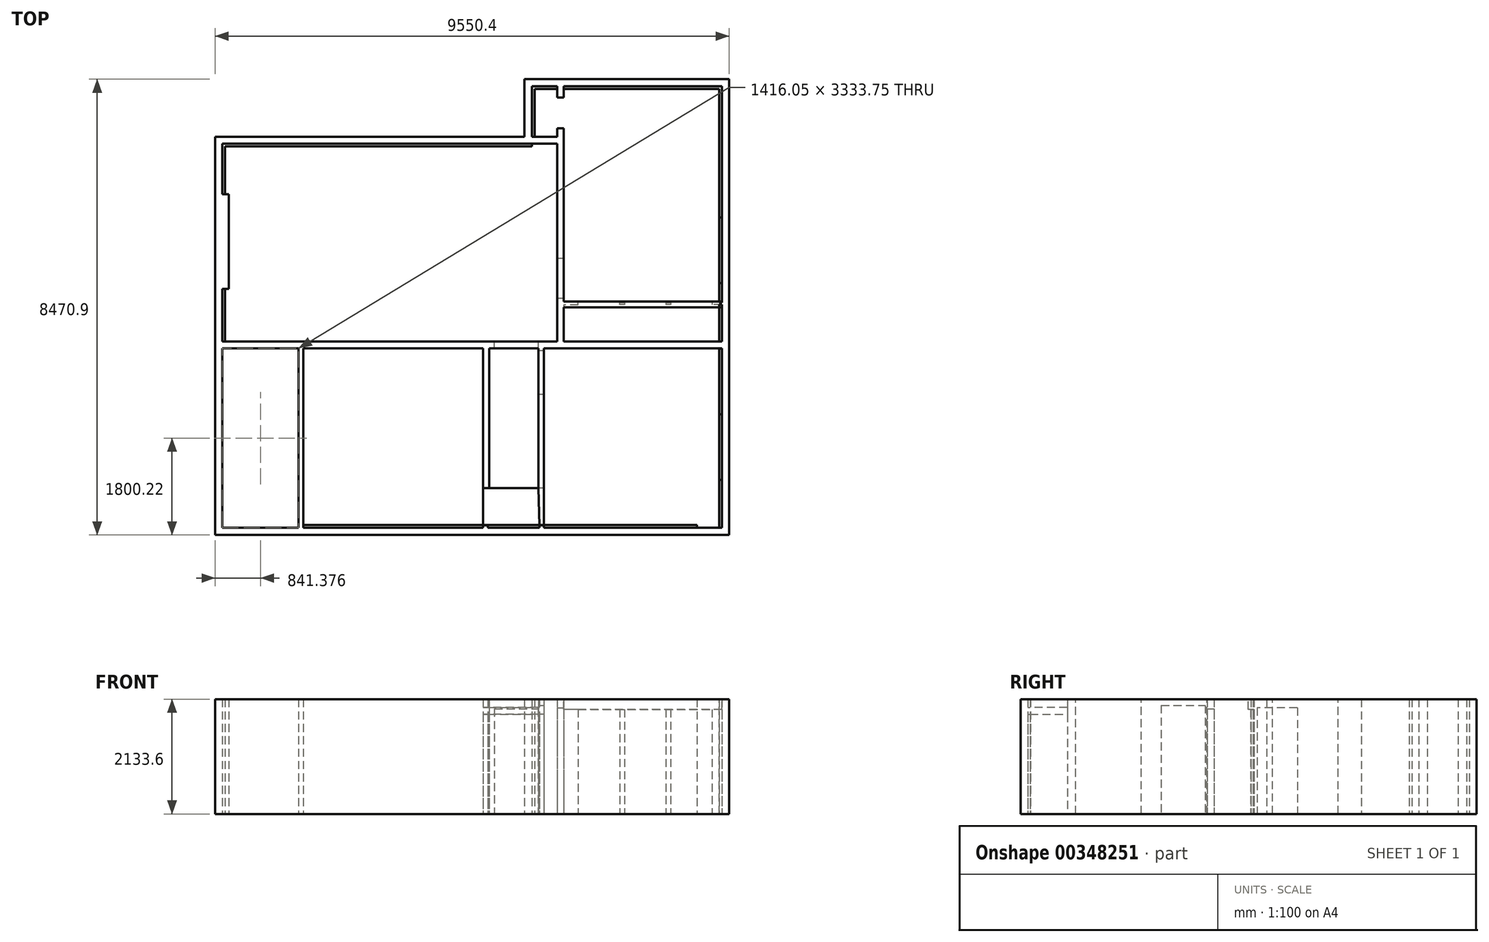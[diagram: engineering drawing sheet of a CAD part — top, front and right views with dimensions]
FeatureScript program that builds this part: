
annotation { "Feature Type Name" : "Feature", "Feature Type Description" : "" }
export const myFeature = defineFeature(function(context is Context, id is Id, definition is map)
    precondition{}
    {
        {
            var Q0;
            Q0=qCreatedBy(makeId("Top.planeOp"),FACE);
            var sketch = newSketch(context, id + "F0", { "sketchPlane" : qUnion([Q0])});
            skLineSegment(sketch, "E0", {"start": v(-2388.66, -7788.34) * mm, "end": v(2665.94, -7788.34) * mm});
            skLineSegment(sketch, "E1", {"start": v(-2388.66, -4111.7) * mm, "end": v(3831.17, -4111.7) * mm});
            skLineSegment(sketch, "E2", {"start": v(-2388.66, -4111.7) * mm, "end": v(-2388.66, -5051.5) * mm});
            skLineSegment(sketch, "E3", {"start": v(-2388.66, -7788.34) * mm, "end": v(-2388.66, -6806) * mm});
            skLineSegment(sketch, "E4", {"start": v(-2388.66, -5051.5) * mm, "end": v(-2269.91, -5051.5) * mm});
            skLineSegment(sketch, "E5", {"start": v(-2388.66, -6806) * mm, "end": v(-2269.91, -6806) * mm});
            skLineSegment(sketch, "E6", {"start": v(-2269.91, -6806) * mm, "end": v(-2269.91, -5051.5) * mm});
            skLineSegment(sketch, "E7", {"start": v(3831.17, -4111.7) * mm, "end": v(3831.17, -6238.94) * mm});
            skLineSegment(sketch, "E8.trimOffspring", {"start": v(3831.17, -4111.7) * mm, "end": v(3831.17, -4111.7) * mm});
            skLineSegment(sketch, "E9", {"start": v(3831.17, -6988.24) * mm, "end": v(3831.17, -7788.34) * mm});
            skLineSegment(sketch, "E10", {"start": v(3478.74, -7788.34) * mm, "end": v(3831.17, -7788.34) * mm});
            skLineSegment(sketch, "E11", {"start": v(3958.17, -6988.24) * mm, "end": v(3831.17, -6988.24) * mm});
            skLineSegment(sketch, "E12", {"start": v(3958.17, -6988.24) * mm, "end": v(3958.17, -7064.44) * mm});
            skLineSegment(sketch, "E13", {"start": v(3958.17, -7064.44) * mm, "end": v(4224.87, -7064.44) * mm});
            skLineSegment(sketch, "E14", {"start": v(6895.04, -7064.44) * mm, "end": v(6895.04, -3044.9) * mm});
            skLineSegment(sketch, "E15", {"start": v(3831.17, -6238.94) * mm, "end": v(3958.17, -6238.94) * mm});
            skLineSegment(sketch, "E16", {"start": v(3958.17, -3044.9) * mm, "end": v(6895.04, -3044.9) * mm});
            skLineSegment(sketch, "E17", {"start": v(3958.17, -3044.9) * mm, "end": v(3958.17, -3254.44) * mm});
            skLineSegment(sketch, "E18", {"start": v(3958.17, -3825.94) * mm, "end": v(3958.17, -6238.94) * mm});
            skLineSegment(sketch, "E19", {"start": v(3958.17, -3254.44) * mm, "end": v(3831.17, -3254.44) * mm});
            skLineSegment(sketch, "E20", {"start": v(3831.17, -3254.44) * mm, "end": v(3831.17, -3044.9) * mm});
            skLineSegment(sketch, "E21", {"start": v(3831.17, -3044.9) * mm, "end": v(3831.17, -3044.9) * mm});
            skLineSegment(sketch, "E22", {"start": v(3831.17, -3044.9) * mm, "end": v(3361.27, -3044.9) * mm});
            skLineSegment(sketch, "E23", {"start": v(3958.17, -3825.94) * mm, "end": v(3831.17, -3825.94) * mm});
            skLineSegment(sketch, "E24", {"start": v(3831.17, -3825.94) * mm, "end": v(3831.17, -3984.7) * mm});
            skLineSegment(sketch, "E25", {"start": v(3361.27, -3044.9) * mm, "end": v(3361.27, -3984.7) * mm});
            skLineSegment(sketch, "E26", {"start": v(3361.27, -3984.7) * mm, "end": v(3831.17, -3984.7) * mm});
            skLineSegment(sketch, "E27", {"start": v(6895.04, -7102.54) * mm, "end": v(6895.04, -7788.34) * mm});
            skLineSegment(sketch, "E28", {"start": v(6895.04, -7102.54) * mm, "end": v(6710.9, -7102.54) * mm});
            skLineSegment(sketch, "E29", {"start": v(3958.17, -7108.9) * mm, "end": v(3958.17, -7788.34) * mm});
            skLineSegment(sketch, "E30", {"start": v(3958.17, -7788.34) * mm, "end": v(6895.04, -7788.34) * mm});
            skLineSegment(sketch, "E31", {"start": v(6710.9, -7064.44) * mm, "end": v(6895.04, -7064.44) * mm});
            skLineSegment(sketch, "E32", {"start": v(6710.9, -7064.44) * mm, "end": v(6710.9, -7102.54) * mm});
            skLineSegment(sketch, "E33", {"start": v(5942.54, -7102.54) * mm, "end": v(5853.64, -7102.54) * mm});
            skLineSegment(sketch, "E34", {"start": v(5942.54, -7064.44) * mm, "end": v(5942.54, -7102.54) * mm});
            skLineSegment(sketch, "E35", {"start": v(5853.64, -7064.44) * mm, "end": v(5942.54, -7064.44) * mm});
            skLineSegment(sketch, "E36", {"start": v(5853.64, -7064.44) * mm, "end": v(5853.64, -7102.54) * mm});
            skLineSegment(sketch, "E37", {"start": v(5085.3, -7102.54) * mm, "end": v(4996.4, -7102.54) * mm});
            skLineSegment(sketch, "E38", {"start": v(4996.4, -7064.44) * mm, "end": v(5085.3, -7064.44) * mm});
            skLineSegment(sketch, "E39", {"start": v(5085.3, -7064.44) * mm, "end": v(5085.3, -7102.54) * mm});
            skLineSegment(sketch, "E40", {"start": v(4996.4, -7102.54) * mm, "end": v(4996.4, -7064.44) * mm});
            skLineSegment(sketch, "E41", {"start": v(4224.87, -7108.9) * mm, "end": v(3958.17, -7108.9) * mm});
            skLineSegment(sketch, "E42", {"start": v(4224.87, -7108.9) * mm, "end": v(4224.87, -7064.44) * mm});
            skLineSegment(sketch, "E43", {"start": v(3478.74, -7788.34) * mm, "end": v(3478.74, -7915.34) * mm});
            skLineSegment(sketch, "E44", {"start": v(3485.1, -7915.34) * mm, "end": v(3478.74, -7915.34) * mm});
            skLineSegment(sketch, "E45", {"start": v(3485.1, -7915.34) * mm, "end": v(3485.1, -7953.44) * mm});
            skLineSegment(sketch, "E46", {"start": v(3485.1, -7953.44) * mm, "end": v(3586.7, -7953.44) * mm});
            skLineSegment(sketch, "E47", {"start": v(3586.7, -7915.34) * mm, "end": v(3586.7, -7953.44) * mm});
            skLineSegment(sketch, "E48", {"start": v(3586.7, -7915.34) * mm, "end": v(6895.04, -7915.34) * mm});
            skLineSegment(sketch, "E49", {"start": v(6895.04, -7915.34) * mm, "end": v(6895.04, -11249.1) * mm});
            skLineSegment(sketch, "E50", {"start": v(6895.04, -11249.1) * mm, "end": v(3586.7, -11249.1) * mm});
            skLineSegment(sketch, "E51", {"start": v(6895.04, -7788.34) * mm, "end": v(6895.04, -7915.34) * mm, "construction": true});
            skLineSegment(sketch, "E52", {"start": v(3586.7, -11249.1) * mm, "end": v(3586.7, -11204.64) * mm});
            skLineSegment(sketch, "E53", {"start": v(3586.7, -8769.42) * mm, "end": v(3586.7, -7953.44) * mm, "construction": true});
            skLineSegment(sketch, "E54", {"start": v(3586.7, -10512.5) * mm, "end": v(3586.7, -8769.42) * mm});
            skLineSegment(sketch, "E55", {"start": v(3586.7, -11204.64) * mm, "end": v(3504.14, -11204.64) * mm});
            skLineSegment(sketch, "E56", {"start": v(3504.14, -11204.64) * mm, "end": v(3504.14, -11249.1) * mm});
            skLineSegment(sketch, "E57", {"start": v(3504.14, -11249.1) * mm, "end": v(2545.3, -11249.1) * mm});
            skLineSegment(sketch, "E58", {"start": v(2545.3, -11249.1) * mm, "end": v(2545.3, -11204.64) * mm});
            skLineSegment(sketch, "E59", {"start": v(2545.3, -11204.64) * mm, "end": v(2456.4, -11204.64) * mm});
            skLineSegment(sketch, "E60", {"start": v(2456.4, -11204.64) * mm, "end": v(2456.4, -11249.1) * mm});
            skLineSegment(sketch, "E61", {"start": v(2456.4, -11249.1) * mm, "end": v(-883.7, -11249.1) * mm});
            skLineSegment(sketch, "E62", {"start": v(-883.7, -11249.1) * mm, "end": v(-883.7, -7915.34) * mm});
            skLineSegment(sketch, "E63", {"start": v(-883.7, -7915.34) * mm, "end": v(2665.94, -7915.34) * mm});
            skLineSegment(sketch, "E64", {"start": v(2665.94, -7915.34) * mm, "end": v(2665.94, -7788.34) * mm});
            skLineSegment(sketch, "E65", {"start": v(3586.7, -8769.42) * mm, "end": v(3485.1, -8769.42) * mm});
            skLineSegment(sketch, "E66", {"start": v(3586.7, -10512.5) * mm, "end": v(3485.1, -10512.5) * mm});
            skLineSegment(sketch, "E67", {"start": v(3485.1, -10512.5) * mm, "end": v(3485.1, -8769.42) * mm});
            skLineSegment(sketch, "E68", {"start": v(3586.7, -11204.64) * mm, "end": v(3586.7, -10512.5) * mm, "construction": true});
            skLineSegment(sketch, "E69", {"start": v(-883.7, -11249.1) * mm, "end": v(-972.6, -11249.1) * mm, "construction": true});
            skLineSegment(sketch, "E70", {"start": v(-972.6, -11249.1) * mm, "end": v(-972.6, -7915.34) * mm});
            skLineSegment(sketch, "E71", {"start": v(-972.6, -7915.34) * mm, "end": v(-2388.66, -7915.34) * mm});
            skLineSegment(sketch, "E72", {"start": v(-2388.66, -7915.34) * mm, "end": v(-2388.66, -11249.1) * mm});
            skLineSegment(sketch, "E73", {"start": v(-2388.66, -11249.1) * mm, "end": v(-972.6, -11249.1) * mm});
            skLineSegment(sketch, "E74", {"start": v(6895.04, -11249.1) * mm, "end": v(6895.04, -11382.44) * mm, "construction": true});
            skLineSegment(sketch, "E75", {"start": v(6895.04, -11249.1) * mm, "end": v(7028.4, -11249.1) * mm, "construction": true});
            skLineSegment(sketch, "E76", {"start": v(7028.4, -11382.44) * mm, "end": v(7028.4, -2911.54) * mm});
            skLineSegment(sketch, "E77", {"start": v(3831.17, -4111.7) * mm, "end": v(3831.17, -3984.7) * mm, "construction": true});
            skLineSegment(sketch, "E78", {"start": v(7028.4, -2911.54) * mm, "end": v(3227.92, -2911.54) * mm});
            skLineSegment(sketch, "E79", {"start": v(3227.92, -2911.54) * mm, "end": v(3227.92, -3984.7) * mm});
            skLineSegment(sketch, "E80", {"start": v(3227.92, -3984.7) * mm, "end": v(-2522, -3984.7) * mm});
            skLineSegment(sketch, "E81", {"start": v(-2522, -3984.7) * mm, "end": v(-2522, -11382.44) * mm});
            skLineSegment(sketch, "E82", {"start": v(-2522, -11382.44) * mm, "end": v(7028.4, -11382.44) * mm});
            skLineSegment(sketch, "E83", {"start": v(2456.4, -10512.5) * mm, "end": v(2456.4, -7915.34) * mm});
            skLineSegment(sketch, "E84", {"start": v(2456.4, -7915.34) * mm, "end": v(2570.7, -7915.34) * mm});
            skLineSegment(sketch, "E85", {"start": v(2570.7, -7915.34) * mm, "end": v(2570.7, -10512.5) * mm});
            skLineSegment(sketch, "E86", {"start": v(2570.7, -10512.5) * mm, "end": v(2456.4, -10512.5) * mm});
            skSolve(sketch);
        }
        {
            var Q0;
            Q0=makeQuery(id+"F0.imprint","IMPRINT",FACE,{"disambiguationData":[TD([[makeQuery(id+"F0.imprint","IMPRINT",EDGE,{"derivedFrom":sQuery(id+"F0.wireOp",EDGE,"E0")}),-1.0]])]});
            extrude(context, id + "F1", {"entities" : qUnion([Q0]), "depth" : 2133.6 * mm, "offsetDistance" : 25.4 * mm});
        }
        {
            var Q0;
            Q0=makeQuery(id+"F0.imprint","IMPRINT",FACE,{"disambiguationData":[TD([[makeQuery(id+"F0.imprint","IMPRINT",EDGE,{"derivedFrom":sQuery(id+"F0.wireOp",EDGE,"E54")}),1.0]])]});
            extrude(context, id + "F2", {"entities" : qUnion([Q0]), "operationType" : NewBodyOperationType.ADD, "depth" : 2133.6 * mm, "offsetDistance" : 25.4 * mm});
        }
        {
            var Q0;
            Q0=makeQuery(id+"F0.imprint","IMPRINT",FACE,{"disambiguationData":[TD([[makeQuery(id+"F0.imprint","IMPRINT",EDGE,{"derivedFrom":sQuery(id+"F0.wireOp",EDGE,"E37")}),-1.0]])]});
            extrude(context, id + "F3", {"entities" : qUnion([Q0]), "operationType" : NewBodyOperationType.ADD, "depth" : 2133.6 * mm, "offsetDistance" : 25.4 * mm});
        }
        {
            var Q0;
            Q0=makeQuery(id+"F0.imprint","IMPRINT",FACE,{"disambiguationData":[TD([[makeQuery(id+"F0.imprint","IMPRINT",EDGE,{"derivedFrom":sQuery(id+"F0.wireOp",EDGE,"E33")}),-1.0]])]});
            extrude(context, id + "F4", {"entities" : qUnion([Q0]), "operationType" : NewBodyOperationType.ADD, "depth" : 2133.6 * mm, "offsetDistance" : 25.4 * mm});
        }
        {
            var Q0;
            Q0=makeQuery(id+"F1.opExtrude","CAP_FACE",FACE,{"disambiguationData":[OSD([sQuery(id+"F0.wireOp",EDGE,"E0"),sQuery(id+"F0.wireOp",EDGE,"E1"),sQuery(id+"F0.wireOp",EDGE,"E2"),sQuery(id+"F0.wireOp",EDGE,"E3"),sQuery(id+"F0.wireOp",EDGE,"E4"),sQuery(id+"F0.wireOp",EDGE,"E5"),sQuery(id+"F0.wireOp",EDGE,"E6"),sQuery(id+"F0.wireOp",EDGE,"E7"),sQuery(id+"F0.wireOp",EDGE,"E9"),sQuery(id+"F0.wireOp",EDGE,"E10"),sQuery(id+"F0.wireOp",EDGE,"E11"),sQuery(id+"F0.wireOp",EDGE,"E12"),sQuery(id+"F0.wireOp",EDGE,"E13"),sQuery(id+"F0.wireOp",EDGE,"E14"),sQuery(id+"F0.wireOp",EDGE,"E15"),sQuery(id+"F0.wireOp",EDGE,"E16"),sQuery(id+"F0.wireOp",EDGE,"E17"),sQuery(id+"F0.wireOp",EDGE,"E18"),sQuery(id+"F0.wireOp",EDGE,"E19"),sQuery(id+"F0.wireOp",EDGE,"E20"),sQuery(id+"F0.wireOp",EDGE,"E22"),sQuery(id+"F0.wireOp",EDGE,"E23"),sQuery(id+"F0.wireOp",EDGE,"E24"),sQuery(id+"F0.wireOp",EDGE,"E25"),sQuery(id+"F0.wireOp",EDGE,"E26"),sQuery(id+"F0.wireOp",EDGE,"E27"),sQuery(id+"F0.wireOp",EDGE,"E28"),sQuery(id+"F0.wireOp",EDGE,"E29"),sQuery(id+"F0.wireOp",EDGE,"E30"),sQuery(id+"F0.wireOp",EDGE,"E31"),sQuery(id+"F0.wireOp",EDGE,"E32"),sQuery(id+"F0.wireOp",EDGE,"E41"),sQuery(id+"F0.wireOp",EDGE,"E42"),sQuery(id+"F0.wireOp",EDGE,"E43"),sQuery(id+"F0.wireOp",EDGE,"E44"),sQuery(id+"F0.wireOp",EDGE,"E45"),sQuery(id+"F0.wireOp",EDGE,"E46"),sQuery(id+"F0.wireOp",EDGE,"E47"),sQuery(id+"F0.wireOp",EDGE,"E48"),sQuery(id+"F0.wireOp",EDGE,"E49"),sQuery(id+"F0.wireOp",EDGE,"E50"),sQuery(id+"F0.wireOp",EDGE,"E52"),sQuery(id+"F0.wireOp",EDGE,"E55"),sQuery(id+"F0.wireOp",EDGE,"E56"),sQuery(id+"F0.wireOp",EDGE,"E57"),sQuery(id+"F0.wireOp",EDGE,"E58"),sQuery(id+"F0.wireOp",EDGE,"E59"),sQuery(id+"F0.wireOp",EDGE,"E60"),sQuery(id+"F0.wireOp",EDGE,"E61"),sQuery(id+"F0.wireOp",EDGE,"E62"),sQuery(id+"F0.wireOp",EDGE,"E63"),sQuery(id+"F0.wireOp",EDGE,"E64"),sQuery(id+"F0.wireOp",EDGE,"E70"),sQuery(id+"F0.wireOp",EDGE,"E71"),sQuery(id+"F0.wireOp",EDGE,"E72"),sQuery(id+"F0.wireOp",EDGE,"E73"),sQuery(id+"F0.wireOp",EDGE,"E76"),sQuery(id+"F0.wireOp",EDGE,"E78"),sQuery(id+"F0.wireOp",EDGE,"E79"),sQuery(id+"F0.wireOp",EDGE,"E80"),sQuery(id+"F0.wireOp",EDGE,"E81"),sQuery(id+"F0.wireOp",EDGE,"E82")])],"isStart":false});
            var sketch = newSketch(context, id + "F5", { "sketchPlane" : qUnion([Q0])});
            skLineSegment(sketch, "E87", {"start": v(3485.1, -7953.44) * mm, "end": v(3586.7, -7953.44) * mm});
            skLineSegment(sketch, "E88", {"start": v(3586.7, -7953.44) * mm, "end": v(3586.7, -8779) * mm});
            skLineSegment(sketch, "E89", {"start": v(3586.7, -8779) * mm, "end": v(3485.1, -8779) * mm});
            skLineSegment(sketch, "E90", {"start": v(3485.1, -8779) * mm, "end": v(3485.1, -7953.44) * mm});
            skSolve(sketch);
        }
        {
            var Q0;
            Q0=makeQuery(id+"F5.imprint","IMPRINT",FACE,{"disambiguationData":[TD([[makeQuery(id+"F5.imprint","IMPRINT",EDGE,{"derivedFrom":sQuery(id+"F5.wireOp",EDGE,"E87")}),-1.0]])]});
            extrude(context, id + "F6", {"entities" : qUnion([Q0]), "operationType" : NewBodyOperationType.ADD, "depth" : -114.3 * mm, "offsetDistance" : 25.4 * mm});
        }
        {
            var Q0;
            Q0=makeQuery(id+"F6.boolean.opBoolean","MERGE",FACE,{"derivedFrom":[makeQuery(id+"F1.opExtrude","CAP_FACE",FACE,{"disambiguationData":[OSD([sQuery(id+"F0.wireOp",EDGE,"E0"),sQuery(id+"F0.wireOp",EDGE,"E1"),sQuery(id+"F0.wireOp",EDGE,"E2"),sQuery(id+"F0.wireOp",EDGE,"E3"),sQuery(id+"F0.wireOp",EDGE,"E4"),sQuery(id+"F0.wireOp",EDGE,"E5"),sQuery(id+"F0.wireOp",EDGE,"E6"),sQuery(id+"F0.wireOp",EDGE,"E7"),sQuery(id+"F0.wireOp",EDGE,"E9"),sQuery(id+"F0.wireOp",EDGE,"E10"),sQuery(id+"F0.wireOp",EDGE,"E11"),sQuery(id+"F0.wireOp",EDGE,"E12"),sQuery(id+"F0.wireOp",EDGE,"E13"),sQuery(id+"F0.wireOp",EDGE,"E14"),sQuery(id+"F0.wireOp",EDGE,"E15"),sQuery(id+"F0.wireOp",EDGE,"E16"),sQuery(id+"F0.wireOp",EDGE,"E17"),sQuery(id+"F0.wireOp",EDGE,"E18"),sQuery(id+"F0.wireOp",EDGE,"E19"),sQuery(id+"F0.wireOp",EDGE,"E20"),sQuery(id+"F0.wireOp",EDGE,"E22"),sQuery(id+"F0.wireOp",EDGE,"E23"),sQuery(id+"F0.wireOp",EDGE,"E24"),sQuery(id+"F0.wireOp",EDGE,"E25"),sQuery(id+"F0.wireOp",EDGE,"E26"),sQuery(id+"F0.wireOp",EDGE,"E27"),sQuery(id+"F0.wireOp",EDGE,"E28"),sQuery(id+"F0.wireOp",EDGE,"E29"),sQuery(id+"F0.wireOp",EDGE,"E30"),sQuery(id+"F0.wireOp",EDGE,"E31"),sQuery(id+"F0.wireOp",EDGE,"E32"),sQuery(id+"F0.wireOp",EDGE,"E41"),sQuery(id+"F0.wireOp",EDGE,"E42"),sQuery(id+"F0.wireOp",EDGE,"E43"),sQuery(id+"F0.wireOp",EDGE,"E44"),sQuery(id+"F0.wireOp",EDGE,"E45"),sQuery(id+"F0.wireOp",EDGE,"E46"),sQuery(id+"F0.wireOp",EDGE,"E47"),sQuery(id+"F0.wireOp",EDGE,"E48"),sQuery(id+"F0.wireOp",EDGE,"E49"),sQuery(id+"F0.wireOp",EDGE,"E50"),sQuery(id+"F0.wireOp",EDGE,"E52"),sQuery(id+"F0.wireOp",EDGE,"E55"),sQuery(id+"F0.wireOp",EDGE,"E56"),sQuery(id+"F0.wireOp",EDGE,"E57"),sQuery(id+"F0.wireOp",EDGE,"E58"),sQuery(id+"F0.wireOp",EDGE,"E59"),sQuery(id+"F0.wireOp",EDGE,"E60"),sQuery(id+"F0.wireOp",EDGE,"E61"),sQuery(id+"F0.wireOp",EDGE,"E62"),sQuery(id+"F0.wireOp",EDGE,"E63"),sQuery(id+"F0.wireOp",EDGE,"E64"),sQuery(id+"F0.wireOp",EDGE,"E70"),sQuery(id+"F0.wireOp",EDGE,"E71"),sQuery(id+"F0.wireOp",EDGE,"E72"),sQuery(id+"F0.wireOp",EDGE,"E73"),sQuery(id+"F0.wireOp",EDGE,"E76"),sQuery(id+"F0.wireOp",EDGE,"E78"),sQuery(id+"F0.wireOp",EDGE,"E79"),sQuery(id+"F0.wireOp",EDGE,"E80"),sQuery(id+"F0.wireOp",EDGE,"E81"),sQuery(id+"F0.wireOp",EDGE,"E82")])],"isStart":false}),makeQuery(id+"F2.opExtrude","CAP_FACE",FACE,{"disambiguationData":[OSD([sQuery(id+"F0.wireOp",EDGE,"E54"),sQuery(id+"F0.wireOp",EDGE,"E65"),sQuery(id+"F0.wireOp",EDGE,"E66"),sQuery(id+"F0.wireOp",EDGE,"E67")])],"isStart":false}),makeQuery(id+"F6.opExtrude","CAP_FACE",FACE,{"disambiguationData":[OSD([sQuery(id+"F5.wireOp",EDGE,"E87"),sQuery(id+"F5.wireOp",EDGE,"E88"),sQuery(id+"F5.wireOp",EDGE,"E89"),sQuery(id+"F5.wireOp",EDGE,"E90")])],"isStart":true})]});
            var sketch = newSketch(context, id + "F7", { "sketchPlane" : qUnion([Q0])});
            skLineSegment(sketch, "E91.bottom", {"start": v(2665.94, -7788.34) * mm, "end": v(3478.74, -7788.34) * mm});
            skLineSegment(sketch, "E91.top", {"start": v(2665.94, -7915.34) * mm, "end": v(3478.74, -7915.34) * mm});
            skLineSegment(sketch, "E91.left", {"start": v(2665.94, -7788.34) * mm, "end": v(2665.94, -7915.34) * mm});
            skLineSegment(sketch, "E91.right", {"start": v(3478.74, -7788.34) * mm, "end": v(3478.74, -7915.34) * mm});
            skSolve(sketch);
        }
        {
            var Q0;
            Q0=makeQuery(id+"F7.imprint","IMPRINT",FACE,{"disambiguationData":[TD([[makeQuery(id+"F7.imprint","IMPRINT",EDGE,{"derivedFrom":sQuery(id+"F7.wireOp",EDGE,"E91.bottom")}),-1.0]])]});
            extrude(context, id + "F8", {"entities" : qUnion([Q0]), "operationType" : NewBodyOperationType.ADD, "depth" : -177.8 * mm, "offsetDistance" : 25.4 * mm});
        }
        {
            var Q0;
            Q0=makeQuery(id+"F8.boolean.opBoolean","MERGE",FACE,{"derivedFrom":[makeQuery(id+"F6.boolean.opBoolean","MERGE",FACE,{"derivedFrom":[makeQuery(id+"F1.opExtrude","CAP_FACE",FACE,{"disambiguationData":[OSD([sQuery(id+"F0.wireOp",EDGE,"E0"),sQuery(id+"F0.wireOp",EDGE,"E1"),sQuery(id+"F0.wireOp",EDGE,"E2"),sQuery(id+"F0.wireOp",EDGE,"E3"),sQuery(id+"F0.wireOp",EDGE,"E4"),sQuery(id+"F0.wireOp",EDGE,"E5"),sQuery(id+"F0.wireOp",EDGE,"E6"),sQuery(id+"F0.wireOp",EDGE,"E7"),sQuery(id+"F0.wireOp",EDGE,"E9"),sQuery(id+"F0.wireOp",EDGE,"E10"),sQuery(id+"F0.wireOp",EDGE,"E11"),sQuery(id+"F0.wireOp",EDGE,"E12"),sQuery(id+"F0.wireOp",EDGE,"E13"),sQuery(id+"F0.wireOp",EDGE,"E14"),sQuery(id+"F0.wireOp",EDGE,"E15"),sQuery(id+"F0.wireOp",EDGE,"E16"),sQuery(id+"F0.wireOp",EDGE,"E17"),sQuery(id+"F0.wireOp",EDGE,"E18"),sQuery(id+"F0.wireOp",EDGE,"E19"),sQuery(id+"F0.wireOp",EDGE,"E20"),sQuery(id+"F0.wireOp",EDGE,"E22"),sQuery(id+"F0.wireOp",EDGE,"E23"),sQuery(id+"F0.wireOp",EDGE,"E24"),sQuery(id+"F0.wireOp",EDGE,"E25"),sQuery(id+"F0.wireOp",EDGE,"E26"),sQuery(id+"F0.wireOp",EDGE,"E27"),sQuery(id+"F0.wireOp",EDGE,"E28"),sQuery(id+"F0.wireOp",EDGE,"E29"),sQuery(id+"F0.wireOp",EDGE,"E30"),sQuery(id+"F0.wireOp",EDGE,"E31"),sQuery(id+"F0.wireOp",EDGE,"E32"),sQuery(id+"F0.wireOp",EDGE,"E41"),sQuery(id+"F0.wireOp",EDGE,"E42"),sQuery(id+"F0.wireOp",EDGE,"E43"),sQuery(id+"F0.wireOp",EDGE,"E44"),sQuery(id+"F0.wireOp",EDGE,"E45"),sQuery(id+"F0.wireOp",EDGE,"E46"),sQuery(id+"F0.wireOp",EDGE,"E47"),sQuery(id+"F0.wireOp",EDGE,"E48"),sQuery(id+"F0.wireOp",EDGE,"E49"),sQuery(id+"F0.wireOp",EDGE,"E50"),sQuery(id+"F0.wireOp",EDGE,"E52"),sQuery(id+"F0.wireOp",EDGE,"E55"),sQuery(id+"F0.wireOp",EDGE,"E56"),sQuery(id+"F0.wireOp",EDGE,"E57"),sQuery(id+"F0.wireOp",EDGE,"E58"),sQuery(id+"F0.wireOp",EDGE,"E59"),sQuery(id+"F0.wireOp",EDGE,"E60"),sQuery(id+"F0.wireOp",EDGE,"E61"),sQuery(id+"F0.wireOp",EDGE,"E62"),sQuery(id+"F0.wireOp",EDGE,"E63"),sQuery(id+"F0.wireOp",EDGE,"E64"),sQuery(id+"F0.wireOp",EDGE,"E70"),sQuery(id+"F0.wireOp",EDGE,"E71"),sQuery(id+"F0.wireOp",EDGE,"E72"),sQuery(id+"F0.wireOp",EDGE,"E73"),sQuery(id+"F0.wireOp",EDGE,"E76"),sQuery(id+"F0.wireOp",EDGE,"E78"),sQuery(id+"F0.wireOp",EDGE,"E79"),sQuery(id+"F0.wireOp",EDGE,"E80"),sQuery(id+"F0.wireOp",EDGE,"E81"),sQuery(id+"F0.wireOp",EDGE,"E82")])],"isStart":false}),makeQuery(id+"F2.opExtrude","CAP_FACE",FACE,{"disambiguationData":[OSD([sQuery(id+"F0.wireOp",EDGE,"E54"),sQuery(id+"F0.wireOp",EDGE,"E65"),sQuery(id+"F0.wireOp",EDGE,"E66"),sQuery(id+"F0.wireOp",EDGE,"E67")])],"isStart":false}),makeQuery(id+"F6.opExtrude","CAP_FACE",FACE,{"disambiguationData":[OSD([sQuery(id+"F5.wireOp",EDGE,"E87"),sQuery(id+"F5.wireOp",EDGE,"E88"),sQuery(id+"F5.wireOp",EDGE,"E89"),sQuery(id+"F5.wireOp",EDGE,"E90")])],"isStart":true})]}),makeQuery(id+"F8.opExtrude","CAP_FACE",FACE,{"disambiguationData":[OSD([sQuery(id+"F7.wireOp",EDGE,"E91.bottom"),sQuery(id+"F7.wireOp",EDGE,"E91.top"),sQuery(id+"F7.wireOp",EDGE,"E91.left"),sQuery(id+"F7.wireOp",EDGE,"E91.right")])],"isStart":true})]});
            var sketch = newSketch(context, id + "F9", { "sketchPlane" : qUnion([Q0])});
            skLineSegment(sketch, "E92.bottom", {"start": v(3831.17, -6238.94) * mm, "end": v(3958.17, -6238.94) * mm});
            skLineSegment(sketch, "E92.top", {"start": v(3831.17, -6988.24) * mm, "end": v(3958.17, -6988.24) * mm});
            skLineSegment(sketch, "E92.left", {"start": v(3831.17, -6238.94) * mm, "end": v(3831.17, -6988.24) * mm});
            skLineSegment(sketch, "E92.right", {"start": v(3958.17, -6238.94) * mm, "end": v(3958.17, -6988.24) * mm});
            skSolve(sketch);
        }
        {
            var Q0;
            Q0=makeQuery(id+"F9.imprint","IMPRINT",FACE,{"disambiguationData":[TD([[makeQuery(id+"F9.imprint","IMPRINT",EDGE,{"derivedFrom":sQuery(id+"F9.wireOp",EDGE,"E92.bottom")}),-1.0]])]});
            extrude(context, id + "F10", {"entities" : qUnion([Q0]), "operationType" : NewBodyOperationType.ADD, "depth" : -158.75 * mm, "offsetDistance" : 25.4 * mm});
        }
        {
            var Q0;
            Q0=makeQuery(id+"F10.boolean.opBoolean","MERGE",FACE,{"derivedFrom":[makeQuery(id+"F8.boolean.opBoolean","MERGE",FACE,{"derivedFrom":[makeQuery(id+"F6.boolean.opBoolean","MERGE",FACE,{"derivedFrom":[makeQuery(id+"F1.opExtrude","CAP_FACE",FACE,{"disambiguationData":[OSD([sQuery(id+"F0.wireOp",EDGE,"E0"),sQuery(id+"F0.wireOp",EDGE,"E1"),sQuery(id+"F0.wireOp",EDGE,"E2"),sQuery(id+"F0.wireOp",EDGE,"E3"),sQuery(id+"F0.wireOp",EDGE,"E4"),sQuery(id+"F0.wireOp",EDGE,"E5"),sQuery(id+"F0.wireOp",EDGE,"E6"),sQuery(id+"F0.wireOp",EDGE,"E7"),sQuery(id+"F0.wireOp",EDGE,"E9"),sQuery(id+"F0.wireOp",EDGE,"E10"),sQuery(id+"F0.wireOp",EDGE,"E11"),sQuery(id+"F0.wireOp",EDGE,"E12"),sQuery(id+"F0.wireOp",EDGE,"E13"),sQuery(id+"F0.wireOp",EDGE,"E14"),sQuery(id+"F0.wireOp",EDGE,"E15"),sQuery(id+"F0.wireOp",EDGE,"E16"),sQuery(id+"F0.wireOp",EDGE,"E17"),sQuery(id+"F0.wireOp",EDGE,"E18"),sQuery(id+"F0.wireOp",EDGE,"E19"),sQuery(id+"F0.wireOp",EDGE,"E20"),sQuery(id+"F0.wireOp",EDGE,"E22"),sQuery(id+"F0.wireOp",EDGE,"E23"),sQuery(id+"F0.wireOp",EDGE,"E24"),sQuery(id+"F0.wireOp",EDGE,"E25"),sQuery(id+"F0.wireOp",EDGE,"E26"),sQuery(id+"F0.wireOp",EDGE,"E27"),sQuery(id+"F0.wireOp",EDGE,"E28"),sQuery(id+"F0.wireOp",EDGE,"E29"),sQuery(id+"F0.wireOp",EDGE,"E30"),sQuery(id+"F0.wireOp",EDGE,"E31"),sQuery(id+"F0.wireOp",EDGE,"E32"),sQuery(id+"F0.wireOp",EDGE,"E41"),sQuery(id+"F0.wireOp",EDGE,"E42"),sQuery(id+"F0.wireOp",EDGE,"E43"),sQuery(id+"F0.wireOp",EDGE,"E44"),sQuery(id+"F0.wireOp",EDGE,"E45"),sQuery(id+"F0.wireOp",EDGE,"E46"),sQuery(id+"F0.wireOp",EDGE,"E47"),sQuery(id+"F0.wireOp",EDGE,"E48"),sQuery(id+"F0.wireOp",EDGE,"E49"),sQuery(id+"F0.wireOp",EDGE,"E50"),sQuery(id+"F0.wireOp",EDGE,"E52"),sQuery(id+"F0.wireOp",EDGE,"E55"),sQuery(id+"F0.wireOp",EDGE,"E56"),sQuery(id+"F0.wireOp",EDGE,"E57"),sQuery(id+"F0.wireOp",EDGE,"E58"),sQuery(id+"F0.wireOp",EDGE,"E59"),sQuery(id+"F0.wireOp",EDGE,"E60"),sQuery(id+"F0.wireOp",EDGE,"E61"),sQuery(id+"F0.wireOp",EDGE,"E62"),sQuery(id+"F0.wireOp",EDGE,"E63"),sQuery(id+"F0.wireOp",EDGE,"E64"),sQuery(id+"F0.wireOp",EDGE,"E70"),sQuery(id+"F0.wireOp",EDGE,"E71"),sQuery(id+"F0.wireOp",EDGE,"E72"),sQuery(id+"F0.wireOp",EDGE,"E73"),sQuery(id+"F0.wireOp",EDGE,"E76"),sQuery(id+"F0.wireOp",EDGE,"E78"),sQuery(id+"F0.wireOp",EDGE,"E79"),sQuery(id+"F0.wireOp",EDGE,"E80"),sQuery(id+"F0.wireOp",EDGE,"E81"),sQuery(id+"F0.wireOp",EDGE,"E82")])],"isStart":false}),makeQuery(id+"F2.opExtrude","CAP_FACE",FACE,{"disambiguationData":[OSD([sQuery(id+"F0.wireOp",EDGE,"E54"),sQuery(id+"F0.wireOp",EDGE,"E65"),sQuery(id+"F0.wireOp",EDGE,"E66"),sQuery(id+"F0.wireOp",EDGE,"E67")])],"isStart":false}),makeQuery(id+"F6.opExtrude","CAP_FACE",FACE,{"disambiguationData":[OSD([sQuery(id+"F5.wireOp",EDGE,"E87"),sQuery(id+"F5.wireOp",EDGE,"E88"),sQuery(id+"F5.wireOp",EDGE,"E89"),sQuery(id+"F5.wireOp",EDGE,"E90")])],"isStart":true})]}),makeQuery(id+"F8.opExtrude","CAP_FACE",FACE,{"disambiguationData":[OSD([sQuery(id+"F7.wireOp",EDGE,"E91.bottom"),sQuery(id+"F7.wireOp",EDGE,"E91.top"),sQuery(id+"F7.wireOp",EDGE,"E91.left"),sQuery(id+"F7.wireOp",EDGE,"E91.right")])],"isStart":true})]}),makeQuery(id+"F10.opExtrude","CAP_FACE",FACE,{"disambiguationData":[OSD([sQuery(id+"F9.wireOp",EDGE,"E92.bottom"),sQuery(id+"F9.wireOp",EDGE,"E92.top"),sQuery(id+"F9.wireOp",EDGE,"E92.left"),sQuery(id+"F9.wireOp",EDGE,"E92.right")])],"isStart":true})]});
            var sketch = newSketch(context, id + "F11", { "sketchPlane" : qUnion([Q0])});
            skLineSegment(sketch, "E93.bottom", {"start": v(6895.04, -7064.44) * mm, "end": v(3958.17, -7064.44) * mm});
            skLineSegment(sketch, "E93.top", {"start": v(6895.04, -7153.34) * mm, "end": v(3958.17, -7153.34) * mm});
            skLineSegment(sketch, "E93.left", {"start": v(6895.04, -7064.44) * mm, "end": v(6895.04, -7153.34) * mm});
            skLineSegment(sketch, "E93.right", {"start": v(3958.17, -7064.44) * mm, "end": v(3958.17, -7153.34) * mm});
            skSolve(sketch);
        }
        {
            var Q0;
            Q0 = qSketchRegion(id + "F11", true);
            extrude(context, id + "F12", {"entities" : qUnion([Q0]), "operationType" : NewBodyOperationType.ADD, "depth" : -190.5 * mm, "offsetDistance" : 25.4 * mm});
        }
        {
            var Q0;
            Q0=makeQuery(id+"F12.boolean.opBoolean","MERGE",FACE,{"derivedFrom":[makeQuery(id+"F1.opExtrude","SWEPT_FACE",FACE,{"disambiguationData":[OSD([sQuery(id+"F0.wireOp",EDGE,"E13")])]}),makeQuery(id+"F1.opExtrude","SWEPT_FACE",FACE,{"disambiguationData":[OSD([sQuery(id+"F0.wireOp",EDGE,"E31")])]}),makeQuery(id+"F3.opExtrude","SWEPT_FACE",FACE,{"disambiguationData":[OSD([sQuery(id+"F0.wireOp",EDGE,"E38")])]}),makeQuery(id+"F4.opExtrude","SWEPT_FACE",FACE,{"disambiguationData":[OSD([sQuery(id+"F0.wireOp",EDGE,"E35")])]}),makeQuery(id+"F12.opExtrude","SWEPT_FACE",FACE,{"disambiguationData":[OSD([sQuery(id+"F11.wireOp",EDGE,"E93.bottom")])]})]});
            var sketch = newSketch(context, id + "F13", { "sketchPlane" : qUnion([Q0])});
            skLineSegment(sketch, "E94", {"start": v(-6710.9, 0) * mm, "end": v(-6895.04, 0) * mm});
            skLineSegment(sketch, "E95", {"start": v(-6895.04, 0) * mm, "end": v(-6895.04, 2133.6) * mm});
            skLineSegment(sketch, "E96", {"start": v(-6895.04, 2133.6) * mm, "end": v(-3958.17, 2133.6) * mm});
            skLineSegment(sketch, "E97", {"start": v(-3958.17, 2133.6) * mm, "end": v(-3958.17, 0) * mm});
            skLineSegment(sketch, "E98", {"start": v(-3958.17, 0) * mm, "end": v(-4224.87, 0) * mm});
            skLineSegment(sketch, "E99", {"start": v(-4224.87, 0) * mm, "end": v(-4224.87, 1943.1) * mm});
            skLineSegment(sketch, "E100", {"start": v(-4224.87, 1943.1) * mm, "end": v(-6710.9, 1943.1) * mm});
            skLineSegment(sketch, "E101", {"start": v(-6710.9, 1943.1) * mm, "end": v(-6710.9, 0) * mm});
            skSolve(sketch);
        }
        {
            var Q0;
            Q0=makeQuery(id+"F13.imprint","IMPRINT",FACE,{"disambiguationData":[TD([[makeQuery(id+"F13.imprint","IMPRINT",EDGE,{"derivedFrom":sQuery(id+"F13.wireOp",EDGE,"E94")}),-1.0]])]});
            extrude(context, id + "F14", {"entities" : qUnion([Q0]), "operationType" : NewBodyOperationType.ADD, "depth" : 19.05 * mm, "offsetDistance" : 25.4 * mm});
        }
        {
            var Q0;
            Q0=makeQuery(id+"F14.boolean.opBoolean","MERGE",FACE,{"derivedFrom":[makeQuery(id+"F12.boolean.opBoolean","MERGE",FACE,{"derivedFrom":[makeQuery(id+"F3.opExtrude","CAP_FACE",FACE,{"disambiguationData":[OSD([sQuery(id+"F0.wireOp",EDGE,"E37"),sQuery(id+"F0.wireOp",EDGE,"E38"),sQuery(id+"F0.wireOp",EDGE,"E39"),sQuery(id+"F0.wireOp",EDGE,"E40")])],"isStart":false}),makeQuery(id+"F4.opExtrude","CAP_FACE",FACE,{"disambiguationData":[OSD([sQuery(id+"F0.wireOp",EDGE,"E33"),sQuery(id+"F0.wireOp",EDGE,"E34"),sQuery(id+"F0.wireOp",EDGE,"E35"),sQuery(id+"F0.wireOp",EDGE,"E36")])],"isStart":false}),makeQuery(id+"F10.boolean.opBoolean","MERGE",FACE,{"derivedFrom":[makeQuery(id+"F8.boolean.opBoolean","MERGE",FACE,{"derivedFrom":[makeQuery(id+"F6.boolean.opBoolean","MERGE",FACE,{"derivedFrom":[makeQuery(id+"F1.opExtrude","CAP_FACE",FACE,{"disambiguationData":[OSD([sQuery(id+"F0.wireOp",EDGE,"E0"),sQuery(id+"F0.wireOp",EDGE,"E1"),sQuery(id+"F0.wireOp",EDGE,"E2"),sQuery(id+"F0.wireOp",EDGE,"E3"),sQuery(id+"F0.wireOp",EDGE,"E4"),sQuery(id+"F0.wireOp",EDGE,"E5"),sQuery(id+"F0.wireOp",EDGE,"E6"),sQuery(id+"F0.wireOp",EDGE,"E7"),sQuery(id+"F0.wireOp",EDGE,"E9"),sQuery(id+"F0.wireOp",EDGE,"E10"),sQuery(id+"F0.wireOp",EDGE,"E11"),sQuery(id+"F0.wireOp",EDGE,"E12"),sQuery(id+"F0.wireOp",EDGE,"E13"),sQuery(id+"F0.wireOp",EDGE,"E14"),sQuery(id+"F0.wireOp",EDGE,"E15"),sQuery(id+"F0.wireOp",EDGE,"E16"),sQuery(id+"F0.wireOp",EDGE,"E17"),sQuery(id+"F0.wireOp",EDGE,"E18"),sQuery(id+"F0.wireOp",EDGE,"E19"),sQuery(id+"F0.wireOp",EDGE,"E20"),sQuery(id+"F0.wireOp",EDGE,"E22"),sQuery(id+"F0.wireOp",EDGE,"E23"),sQuery(id+"F0.wireOp",EDGE,"E24"),sQuery(id+"F0.wireOp",EDGE,"E25"),sQuery(id+"F0.wireOp",EDGE,"E26"),sQuery(id+"F0.wireOp",EDGE,"E27"),sQuery(id+"F0.wireOp",EDGE,"E28"),sQuery(id+"F0.wireOp",EDGE,"E29"),sQuery(id+"F0.wireOp",EDGE,"E30"),sQuery(id+"F0.wireOp",EDGE,"E31"),sQuery(id+"F0.wireOp",EDGE,"E32"),sQuery(id+"F0.wireOp",EDGE,"E41"),sQuery(id+"F0.wireOp",EDGE,"E42"),sQuery(id+"F0.wireOp",EDGE,"E43"),sQuery(id+"F0.wireOp",EDGE,"E44"),sQuery(id+"F0.wireOp",EDGE,"E45"),sQuery(id+"F0.wireOp",EDGE,"E46"),sQuery(id+"F0.wireOp",EDGE,"E47"),sQuery(id+"F0.wireOp",EDGE,"E48"),sQuery(id+"F0.wireOp",EDGE,"E49"),sQuery(id+"F0.wireOp",EDGE,"E50"),sQuery(id+"F0.wireOp",EDGE,"E52"),sQuery(id+"F0.wireOp",EDGE,"E55"),sQuery(id+"F0.wireOp",EDGE,"E56"),sQuery(id+"F0.wireOp",EDGE,"E57"),sQuery(id+"F0.wireOp",EDGE,"E58"),sQuery(id+"F0.wireOp",EDGE,"E59"),sQuery(id+"F0.wireOp",EDGE,"E60"),sQuery(id+"F0.wireOp",EDGE,"E61"),sQuery(id+"F0.wireOp",EDGE,"E62"),sQuery(id+"F0.wireOp",EDGE,"E63"),sQuery(id+"F0.wireOp",EDGE,"E64"),sQuery(id+"F0.wireOp",EDGE,"E70"),sQuery(id+"F0.wireOp",EDGE,"E71"),sQuery(id+"F0.wireOp",EDGE,"E72"),sQuery(id+"F0.wireOp",EDGE,"E73"),sQuery(id+"F0.wireOp",EDGE,"E76"),sQuery(id+"F0.wireOp",EDGE,"E78"),sQuery(id+"F0.wireOp",EDGE,"E79"),sQuery(id+"F0.wireOp",EDGE,"E80"),sQuery(id+"F0.wireOp",EDGE,"E81"),sQuery(id+"F0.wireOp",EDGE,"E82")])],"isStart":false}),makeQuery(id+"F2.opExtrude","CAP_FACE",FACE,{"disambiguationData":[OSD([sQuery(id+"F0.wireOp",EDGE,"E54"),sQuery(id+"F0.wireOp",EDGE,"E65"),sQuery(id+"F0.wireOp",EDGE,"E66"),sQuery(id+"F0.wireOp",EDGE,"E67")])],"isStart":false}),makeQuery(id+"F6.opExtrude","CAP_FACE",FACE,{"disambiguationData":[OSD([sQuery(id+"F5.wireOp",EDGE,"E87"),sQuery(id+"F5.wireOp",EDGE,"E88"),sQuery(id+"F5.wireOp",EDGE,"E89"),sQuery(id+"F5.wireOp",EDGE,"E90")])],"isStart":true})]}),makeQuery(id+"F8.opExtrude","CAP_FACE",FACE,{"disambiguationData":[OSD([sQuery(id+"F7.wireOp",EDGE,"E91.bottom"),sQuery(id+"F7.wireOp",EDGE,"E91.top"),sQuery(id+"F7.wireOp",EDGE,"E91.left"),sQuery(id+"F7.wireOp",EDGE,"E91.right")])],"isStart":true})]}),makeQuery(id+"F10.opExtrude","CAP_FACE",FACE,{"disambiguationData":[OSD([sQuery(id+"F9.wireOp",EDGE,"E92.bottom"),sQuery(id+"F9.wireOp",EDGE,"E92.top"),sQuery(id+"F9.wireOp",EDGE,"E92.left"),sQuery(id+"F9.wireOp",EDGE,"E92.right")])],"isStart":true})]}),makeQuery(id+"F12.opExtrude","CAP_FACE",FACE,{"disambiguationData":[OSD([sQuery(id+"F11.wireOp",EDGE,"E93.bottom"),sQuery(id+"F11.wireOp",EDGE,"E93.top"),sQuery(id+"F11.wireOp",EDGE,"E93.left"),sQuery(id+"F11.wireOp",EDGE,"E93.right")])],"isStart":true})]}),makeQuery(id+"F14.opExtrude","SWEPT_FACE",FACE,{"disambiguationData":[OSD([sQuery(id+"F13.wireOp",EDGE,"E96")])]})]});
            var sketch = newSketch(context, id + "F15", { "sketchPlane" : qUnion([Q0])});
            skLineSegment(sketch, "E102", {"start": v(3586.7, -11204.64) * mm, "end": v(3586.7, -10512.5) * mm});
            skLineSegment(sketch, "E103", {"start": v(3586.7, -10512.5) * mm, "end": v(3485.1, -10512.5) * mm});
            skLineSegment(sketch, "E104", {"start": v(3485.1, -10512.5) * mm, "end": v(3504.14, -11204.64) * mm});
            skLineSegment(sketch, "E105", {"start": v(3504.14, -11204.64) * mm, "end": v(3586.7, -11204.64) * mm});
            skSolve(sketch);
        }
        {
            var Q0;
            Q0=makeQuery(id+"F15.imprint","IMPRINT",FACE,{"disambiguationData":[TD([[makeQuery(id+"F15.imprint","IMPRINT",EDGE,{"derivedFrom":sQuery(id+"F15.wireOp",EDGE,"E102")}),1.0]])]});
            extrude(context, id + "F16", {"entities" : qUnion([Q0]), "operationType" : NewBodyOperationType.ADD, "depth" : -279.4 * mm, "offsetDistance" : 25.4 * mm});
        }
        {
            var Q0;
            Q0=makeQuery(id+"F16.opExtrude","CAP_FACE",FACE,{"disambiguationData":[OSD([sQuery(id+"F15.wireOp",EDGE,"E102"),sQuery(id+"F15.wireOp",EDGE,"E103"),sQuery(id+"F15.wireOp",EDGE,"E104"),sQuery(id+"F15.wireOp",EDGE,"E105")])],"isStart":false});
            var sketch = newSketch(context, id + "F17", { "sketchPlane" : qUnion([Q0])});
            skLineSegment(sketch, "E106.bottom", {"start": v(3586.7, 10512.5) * mm, "end": v(2456.4, 10512.5) * mm});
            skLineSegment(sketch, "E106.top", {"start": v(3586.7, 11376.1) * mm, "end": v(2456.4, 11376.1) * mm});
            skLineSegment(sketch, "E106.left", {"start": v(3586.7, 10512.5) * mm, "end": v(3586.7, 11376.1) * mm});
            skLineSegment(sketch, "E106.right", {"start": v(2456.4, 10512.5) * mm, "end": v(2456.4, 11376.1) * mm});
            skSolve(sketch);
        }
        {
            var Q0;
            {var subQ2=sQuery(id+"F17.wireOp",EDGE,"E106.top");Q0=makeQuery(id+"F17.imprint","IMPRINT",FACE,{"disambiguationData":[TD([[makeQuery(id+"F17.imprint","IMPRINT",EDGE,{"derivedFrom":subQ2}),1.0]])]});}
            extrude(context, id + "F18", {"entities" : qUnion([Q0]), "operationType" : NewBodyOperationType.ADD, "depth" : -127 * mm, "offsetDistance" : 25.4 * mm});
        }
        {
            var Q0;
            {var subQ0=sQuery(id+"F0.wireOp",EDGE,"E83");Q0=makeQuery(id+"F0.imprint","IMPRINT",FACE,{"disambiguationData":[TD([[makeQuery(id+"F0.imprint","IMPRINT",EDGE,{"derivedFrom":subQ0}),-1.0]])]});}
            extrude(context, id + "F19", {"entities" : qUnion([Q0]), "operationType" : NewBodyOperationType.ADD, "depth" : 2133.6 * mm, "offsetDistance" : 25.4 * mm});
        }
        {
            var Q0;
            Q0=makeQuery(id+"F0.imprint","IMPRINT",FACE,{"disambiguationData":[TD([[makeQuery(id+"F0.imprint","IMPRINT",EDGE,{"derivedFrom":sQuery(id+"F0.wireOp",EDGE,"E0")}),-1.0]])]});
            var sketch = newSketch(context, id + "F20", { "sketchPlane" : qUnion([Q0])});
            skLineSegment(sketch, "E107.bottom", {"start": v(-2388.66, -4162.5) * mm, "end": v(-1169.46, -4162.5) * mm});
            skLineSegment(sketch, "E107.top", {"start": v(-2388.66, -4111.7) * mm, "end": v(-1169.46, -4111.7) * mm});
            skLineSegment(sketch, "E107.left", {"start": v(-2388.66, -4162.5) * mm, "end": v(-2388.66, -4111.7) * mm});
            skLineSegment(sketch, "E107.right", {"start": v(-1169.46, -4162.5) * mm, "end": v(-1169.46, -4111.7) * mm});
            skLineSegment(sketch, "E108.bottom", {"start": v(-1169.46, -4162.5) * mm, "end": v(49.74, -4162.5) * mm});
            skLineSegment(sketch, "E108.top", {"start": v(-1169.46, -4111.7) * mm, "end": v(49.74, -4111.7) * mm});
            skLineSegment(sketch, "E108.right", {"start": v(49.74, -4162.5) * mm, "end": v(49.74, -4111.7) * mm});
            skLineSegment(sketch, "E109.bottom", {"start": v(49.74, -4162.5) * mm, "end": v(1268.94, -4162.5) * mm});
            skLineSegment(sketch, "E109.top", {"start": v(49.74, -4111.7) * mm, "end": v(1268.94, -4111.7) * mm});
            skLineSegment(sketch, "E109.right", {"start": v(1268.94, -4162.5) * mm, "end": v(1268.94, -4111.7) * mm});
            skLineSegment(sketch, "E110.bottom", {"start": v(1268.94, -4162.5) * mm, "end": v(2488.14, -4162.5) * mm});
            skLineSegment(sketch, "E110.top", {"start": v(1268.94, -4111.7) * mm, "end": v(2488.14, -4111.7) * mm});
            skLineSegment(sketch, "E110.right", {"start": v(2488.14, -4162.5) * mm, "end": v(2488.14, -4111.7) * mm});
            skLineSegment(sketch, "E111.bottom", {"start": v(2488.14, -4162.5) * mm, "end": v(3707.34, -4162.5) * mm});
            skLineSegment(sketch, "E111.top", {"start": v(2488.14, -4111.7) * mm, "end": v(3707.34, -4111.7) * mm});
            skLineSegment(sketch, "E111.right", {"start": v(3707.34, -4162.5) * mm, "end": v(3707.34, -4111.7) * mm});
            skLineSegment(sketch, "E112.bottom", {"start": v(3412.07, -4264.1) * mm, "end": v(3412.07, -3044.9) * mm});
            skLineSegment(sketch, "E112.top", {"start": v(3361.27, -4264.1) * mm, "end": v(3361.27, -3044.9) * mm});
            skLineSegment(sketch, "E112.left", {"start": v(3412.07, -4264.1) * mm, "end": v(3361.27, -4264.1) * mm});
            skLineSegment(sketch, "E112.right", {"start": v(3412.07, -3044.9) * mm, "end": v(3361.27, -3044.9) * mm});
            skLineSegment(sketch, "E113.bottom", {"start": v(3412.07, -3095.7) * mm, "end": v(4631.27, -3095.7) * mm});
            skLineSegment(sketch, "E113.top", {"start": v(3412.07, -3044.9) * mm, "end": v(4631.27, -3044.9) * mm});
            skLineSegment(sketch, "E113.left", {"start": v(3412.07, -3095.7) * mm, "end": v(3412.07, -3044.9) * mm});
            skLineSegment(sketch, "E113.right", {"start": v(4631.27, -3095.7) * mm, "end": v(4631.27, -3044.9) * mm});
            skLineSegment(sketch, "E114.bottom", {"start": v(4631.27, -3095.7) * mm, "end": v(5850.47, -3095.7) * mm});
            skLineSegment(sketch, "E114.top", {"start": v(4631.27, -3044.9) * mm, "end": v(5850.47, -3044.9) * mm});
            skLineSegment(sketch, "E114.right", {"start": v(5850.47, -3095.7) * mm, "end": v(5850.47, -3044.9) * mm});
            skLineSegment(sketch, "E115.bottom", {"start": v(5850.47, -3095.7) * mm, "end": v(7069.67, -3095.7) * mm});
            skLineSegment(sketch, "E115.top", {"start": v(5850.47, -3044.9) * mm, "end": v(7069.67, -3044.9) * mm});
            skLineSegment(sketch, "E115.right", {"start": v(7069.67, -3095.7) * mm, "end": v(7069.67, -3044.9) * mm});
            skLineSegment(sketch, "E116.bottom", {"start": v(6844.24, -4264.1) * mm, "end": v(6844.24, -3044.9) * mm});
            skLineSegment(sketch, "E116.top", {"start": v(6895.04, -4264.1) * mm, "end": v(6895.04, -3044.9) * mm});
            skLineSegment(sketch, "E116.left", {"start": v(6844.24, -4264.1) * mm, "end": v(6895.04, -4264.1) * mm});
            skLineSegment(sketch, "E116.right", {"start": v(6844.24, -3044.9) * mm, "end": v(6895.04, -3044.9) * mm});
            skLineSegment(sketch, "E117.bottom", {"start": v(6844.24, -5483.3) * mm, "end": v(6844.24, -4264.1) * mm});
            skLineSegment(sketch, "E117.top", {"start": v(6895.04, -5483.3) * mm, "end": v(6895.04, -4264.1) * mm});
            skLineSegment(sketch, "E117.left", {"start": v(6844.24, -5483.3) * mm, "end": v(6895.04, -5483.3) * mm});
            skLineSegment(sketch, "E118.0.1.0", {"start": v(6844.24, -6702.5) * mm, "end": v(6895.04, -6702.5) * mm});
            skLineSegment(sketch, "E118.0.1.2", {"start": v(6844.24, -6702.5) * mm, "end": v(6844.24, -5483.3) * mm});
            skLineSegment(sketch, "E118.0.1.3", {"start": v(6895.04, -6702.5) * mm, "end": v(6895.04, -5483.3) * mm});
            skLineSegment(sketch, "E118.0.2.0", {"start": v(6844.24, -7921.7) * mm, "end": v(6895.04, -7921.7) * mm});
            skLineSegment(sketch, "E118.0.2.1", {"start": v(6844.24, -6702.5) * mm, "end": v(6895.04, -6702.5) * mm});
            skLineSegment(sketch, "E118.0.2.2", {"start": v(6844.24, -7921.7) * mm, "end": v(6844.24, -6702.5) * mm});
            skLineSegment(sketch, "E118.0.2.3", {"start": v(6895.04, -7921.7) * mm, "end": v(6895.04, -6702.5) * mm});
            skLineSegment(sketch, "E118.0.3.0", {"start": v(6844.24, -9140.89) * mm, "end": v(6895.04, -9140.89) * mm});
            skLineSegment(sketch, "E118.0.3.1", {"start": v(6844.24, -7921.69) * mm, "end": v(6895.04, -7921.69) * mm});
            skLineSegment(sketch, "E118.0.3.2", {"start": v(6844.24, -9140.89) * mm, "end": v(6844.24, -7921.69) * mm});
            skLineSegment(sketch, "E118.0.3.3", {"start": v(6895.04, -9140.89) * mm, "end": v(6895.04, -7921.69) * mm});
            skLineSegment(sketch, "E118.1.1.0", {"start": v(6844.24, -6702.5) * mm, "end": v(6895.04, -6702.5) * mm});
            skLineSegment(sketch, "E118.1.1.2", {"start": v(6844.24, -6702.5) * mm, "end": v(6844.24, -5483.3) * mm});
            skLineSegment(sketch, "E118.1.1.3", {"start": v(6895.04, -6702.5) * mm, "end": v(6895.04, -5483.3) * mm});
            skLineSegment(sketch, "E118.1.2.0", {"start": v(6844.24, -7921.7) * mm, "end": v(6895.04, -7921.7) * mm});
            skLineSegment(sketch, "E118.1.2.1", {"start": v(6844.24, -6702.5) * mm, "end": v(6895.04, -6702.5) * mm});
            skLineSegment(sketch, "E118.1.2.2", {"start": v(6844.24, -7921.7) * mm, "end": v(6844.24, -6702.5) * mm});
            skLineSegment(sketch, "E118.1.2.3", {"start": v(6895.04, -7921.7) * mm, "end": v(6895.04, -6702.5) * mm});
            skLineSegment(sketch, "E118.1.3.0", {"start": v(6844.24, -9140.89) * mm, "end": v(6895.04, -9140.89) * mm});
            skLineSegment(sketch, "E118.1.3.1", {"start": v(6844.24, -7921.69) * mm, "end": v(6895.04, -7921.69) * mm});
            skLineSegment(sketch, "E118.1.3.2", {"start": v(6844.24, -9140.89) * mm, "end": v(6844.24, -7921.69) * mm});
            skLineSegment(sketch, "E118.1.3.3", {"start": v(6895.04, -9140.89) * mm, "end": v(6895.04, -7921.69) * mm});
            skLineSegment(sketch, "E118.2.1.0", {"start": v(6844.24, -6702.5) * mm, "end": v(6895.04, -6702.5) * mm});
            skLineSegment(sketch, "E118.2.1.2", {"start": v(6844.24, -6702.5) * mm, "end": v(6844.24, -5483.3) * mm});
            skLineSegment(sketch, "E118.2.1.3", {"start": v(6895.04, -6702.5) * mm, "end": v(6895.04, -5483.3) * mm});
            skLineSegment(sketch, "E118.2.2.0", {"start": v(6844.24, -7921.7) * mm, "end": v(6895.04, -7921.7) * mm});
            skLineSegment(sketch, "E118.2.2.1", {"start": v(6844.24, -6702.5) * mm, "end": v(6895.04, -6702.5) * mm});
            skLineSegment(sketch, "E118.2.2.2", {"start": v(6844.24, -7921.7) * mm, "end": v(6844.24, -6702.5) * mm});
            skLineSegment(sketch, "E118.2.2.3", {"start": v(6895.04, -7921.7) * mm, "end": v(6895.04, -6702.5) * mm});
            skLineSegment(sketch, "E118.2.3.0", {"start": v(6844.24, -9140.89) * mm, "end": v(6895.04, -9140.89) * mm});
            skLineSegment(sketch, "E118.2.3.1", {"start": v(6844.24, -7921.69) * mm, "end": v(6895.04, -7921.69) * mm});
            skLineSegment(sketch, "E118.2.3.2", {"start": v(6844.24, -9140.89) * mm, "end": v(6844.24, -7921.69) * mm});
            skLineSegment(sketch, "E118.2.3.3", {"start": v(6895.04, -9140.89) * mm, "end": v(6895.04, -7921.69) * mm});
            skLineSegment(sketch, "E118.direction1", {"start": v(6844.24, -5483.3) * mm, "end": v(6844.24, -5483.3) * mm});
            skLineSegment(sketch, "E118.direction2", {"start": v(6844.24, -5483.3) * mm, "end": v(6844.24, -6702.5) * mm, "construction": true});
            skLineSegment(sketch, "E119.0.0.4", {"start": v(6844.24, -10360.09) * mm, "end": v(6895.04, -10360.09) * mm});
            skLineSegment(sketch, "E119.6.0.4", {"start": v(6844.24, -10360.09) * mm, "end": v(6844.24, -9140.89) * mm});
            skLineSegment(sketch, "E119.9.0.4", {"start": v(6895.04, -10360.09) * mm, "end": v(6895.04, -9140.89) * mm});
            skLineSegment(sketch, "E119.0.0.5", {"start": v(6844.24, -11579.29) * mm, "end": v(6895.04, -11579.29) * mm});
            skLineSegment(sketch, "E119.3.0.5", {"start": v(6844.24, -10360.09) * mm, "end": v(6895.04, -10360.09) * mm});
            skLineSegment(sketch, "E119.6.0.5", {"start": v(6844.24, -11579.29) * mm, "end": v(6844.24, -10360.09) * mm});
            skLineSegment(sketch, "E119.9.0.5", {"start": v(6895.04, -11579.29) * mm, "end": v(6895.04, -10360.09) * mm});
            skLineSegment(sketch, "E119.0.1.4", {"start": v(6844.24, -10360.09) * mm, "end": v(6895.04, -10360.09) * mm});
            skLineSegment(sketch, "E119.6.1.4", {"start": v(6844.24, -10360.09) * mm, "end": v(6844.24, -9140.89) * mm});
            skLineSegment(sketch, "E119.9.1.4", {"start": v(6895.04, -10360.09) * mm, "end": v(6895.04, -9140.89) * mm});
            skLineSegment(sketch, "E119.0.1.5", {"start": v(6844.24, -11579.29) * mm, "end": v(6895.04, -11579.29) * mm});
            skLineSegment(sketch, "E119.3.1.5", {"start": v(6844.24, -10360.09) * mm, "end": v(6895.04, -10360.09) * mm});
            skLineSegment(sketch, "E119.6.1.5", {"start": v(6844.24, -11579.29) * mm, "end": v(6844.24, -10360.09) * mm});
            skLineSegment(sketch, "E119.9.1.5", {"start": v(6895.04, -11579.29) * mm, "end": v(6895.04, -10360.09) * mm});
            skLineSegment(sketch, "E119.0.2.4", {"start": v(6844.24, -10360.09) * mm, "end": v(6895.04, -10360.09) * mm});
            skLineSegment(sketch, "E119.6.2.4", {"start": v(6844.24, -10360.09) * mm, "end": v(6844.24, -9140.89) * mm});
            skLineSegment(sketch, "E119.9.2.4", {"start": v(6895.04, -10360.09) * mm, "end": v(6895.04, -9140.89) * mm});
            skLineSegment(sketch, "E119.0.2.5", {"start": v(6844.24, -11579.29) * mm, "end": v(6895.04, -11579.29) * mm});
            skLineSegment(sketch, "E119.3.2.5", {"start": v(6844.24, -10360.09) * mm, "end": v(6895.04, -10360.09) * mm});
            skLineSegment(sketch, "E119.6.2.5", {"start": v(6844.24, -11579.29) * mm, "end": v(6844.24, -10360.09) * mm});
            skLineSegment(sketch, "E119.9.2.5", {"start": v(6895.04, -11579.29) * mm, "end": v(6895.04, -10360.09) * mm});
            skLineSegment(sketch, "E120.bottom", {"start": v(-883.7, -11198.3) * mm, "end": v(335.5, -11198.3) * mm});
            skLineSegment(sketch, "E120.top", {"start": v(-883.7, -11249.1) * mm, "end": v(335.5, -11249.1) * mm});
            skLineSegment(sketch, "E120.left", {"start": v(-883.7, -11198.3) * mm, "end": v(-883.7, -11249.1) * mm});
            skLineSegment(sketch, "E120.right", {"start": v(335.5, -11198.3) * mm, "end": v(335.5, -11249.1) * mm});
            skLineSegment(sketch, "E121.1.0.0", {"start": v(335.5, -11198.3) * mm, "end": v(1554.7, -11198.3) * mm});
            skLineSegment(sketch, "E121.1.0.1", {"start": v(1554.7, -11198.3) * mm, "end": v(1554.7, -11249.1) * mm});
            skLineSegment(sketch, "E121.1.0.2", {"start": v(335.5, -11249.1) * mm, "end": v(1554.7, -11249.1) * mm});
            skLineSegment(sketch, "E121.2.0.0", {"start": v(1554.7, -11198.3) * mm, "end": v(2773.9, -11198.3) * mm});
            skLineSegment(sketch, "E121.2.0.1", {"start": v(2773.9, -11198.3) * mm, "end": v(2773.9, -11249.1) * mm});
            skLineSegment(sketch, "E121.2.0.2", {"start": v(1554.7, -11249.1) * mm, "end": v(2773.9, -11249.1) * mm});
            skLineSegment(sketch, "E121.2.0.3", {"start": v(1554.7, -11198.3) * mm, "end": v(1554.7, -11249.1) * mm});
            skLineSegment(sketch, "E121.3.0.0", {"start": v(2773.9, -11198.3) * mm, "end": v(3993.1, -11198.3) * mm});
            skLineSegment(sketch, "E121.3.0.1", {"start": v(3993.1, -11198.3) * mm, "end": v(3993.1, -11249.1) * mm});
            skLineSegment(sketch, "E121.3.0.2", {"start": v(2773.9, -11249.1) * mm, "end": v(3993.1, -11249.1) * mm});
            skLineSegment(sketch, "E121.3.0.3", {"start": v(2773.9, -11198.3) * mm, "end": v(2773.9, -11249.1) * mm});
            skLineSegment(sketch, "E121.4.0.0", {"start": v(3993.1, -11198.3) * mm, "end": v(5212.3, -11198.3) * mm});
            skLineSegment(sketch, "E121.4.0.1", {"start": v(5212.3, -11198.3) * mm, "end": v(5212.3, -11249.1) * mm});
            skLineSegment(sketch, "E121.4.0.2", {"start": v(3993.1, -11249.1) * mm, "end": v(5212.3, -11249.1) * mm});
            skLineSegment(sketch, "E121.4.0.3", {"start": v(3993.1, -11198.3) * mm, "end": v(3993.1, -11249.1) * mm});
            skLineSegment(sketch, "E121.5.0.0", {"start": v(5212.3, -11198.3) * mm, "end": v(6431.5, -11198.3) * mm});
            skLineSegment(sketch, "E121.5.0.1", {"start": v(6431.5, -11198.3) * mm, "end": v(6431.5, -11249.1) * mm});
            skLineSegment(sketch, "E121.5.0.2", {"start": v(5212.3, -11249.1) * mm, "end": v(6431.5, -11249.1) * mm});
            skLineSegment(sketch, "E121.5.0.3", {"start": v(5212.3, -11198.3) * mm, "end": v(5212.3, -11249.1) * mm});
            skLineSegment(sketch, "E121.direction1", {"start": v(-883.7, -11249.1) * mm, "end": v(335.5, -11249.1) * mm, "construction": true});
            skLineSegment(sketch, "E122.bottom", {"start": v(-2388.66, -5381.7) * mm, "end": v(-2388.66, -4162.5) * mm});
            skLineSegment(sketch, "E122.top", {"start": v(-2337.86, -5381.7) * mm, "end": v(-2337.86, -4162.5) * mm});
            skLineSegment(sketch, "E122.left", {"start": v(-2388.66, -5381.7) * mm, "end": v(-2337.86, -5381.7) * mm});
            skLineSegment(sketch, "E122.right", {"start": v(-2388.66, -4162.5) * mm, "end": v(-2337.86, -4162.5) * mm});
            skLineSegment(sketch, "E123.bottom", {"start": v(-2388.66, -7788.34) * mm, "end": v(-2388.66, -6569.14) * mm});
            skLineSegment(sketch, "E123.top", {"start": v(-2337.86, -7788.34) * mm, "end": v(-2337.86, -6569.14) * mm});
            skLineSegment(sketch, "E123.left", {"start": v(-2388.66, -7788.34) * mm, "end": v(-2337.86, -7788.34) * mm});
            skLineSegment(sketch, "E123.right", {"start": v(-2388.66, -6569.14) * mm, "end": v(-2337.86, -6569.14) * mm});
            skSolve(sketch);
        }
        {
            var Q0;
            {var subQ0=sQuery(id+"F20.wireOp",EDGE,"E122.top");var subQ1=sQuery(id+"F20.wireOp",EDGE,"E107.bottom");var subQ2=makeQuery(id+"F20.imprint","INTERSECT",VERTEX,{"derivedFrom":[subQ1,subQ0]});Q0=makeQuery(id+"F20.imprint","IMPRINT",FACE,{"disambiguationData":[TD([[makeQuery(id+"F20.imprint","IMPRINT",EDGE,{"disambiguationData":[TD([[subQ2,1.0]])],"derivedFrom":subQ0}),1.0]])]});}
            var Q1;
            Q1=makeQuery(id+"F20.imprint","IMPRINT",FACE,{"disambiguationData":[TD([[makeQuery(id+"F20.imprint","IMPRINT",EDGE,{"derivedFrom":sQuery(id+"F20.wireOp",EDGE,"E107.top")}),-1.0]])]});
            var Q2;
            Q2=makeQuery(id+"F20.imprint","IMPRINT",FACE,{"disambiguationData":[TD([[makeQuery(id+"F20.imprint","IMPRINT",EDGE,{"derivedFrom":sQuery(id+"F20.wireOp",EDGE,"E107.right")}),-1.0]])]});
            var Q3;
            Q3=makeQuery(id+"F20.imprint","IMPRINT",FACE,{"disambiguationData":[TD([[makeQuery(id+"F20.imprint","IMPRINT",EDGE,{"derivedFrom":sQuery(id+"F20.wireOp",EDGE,"E108.right")}),-1.0]])]});
            var Q4;
            Q4=makeQuery(id+"F20.imprint","IMPRINT",FACE,{"disambiguationData":[TD([[makeQuery(id+"F20.imprint","IMPRINT",EDGE,{"derivedFrom":sQuery(id+"F20.wireOp",EDGE,"E109.right")}),-1.0]])]});
            var Q5;
            {var subQ0=sQuery(id+"F20.wireOp",EDGE,"E110.right");Q5=makeQuery(id+"F20.imprint","IMPRINT",FACE,{"disambiguationData":[TD([[makeQuery(id+"F20.imprint","IMPRINT",EDGE,{"derivedFrom":subQ0}),-1.0]])]});}
            var Q6;
            {var subQ0=sQuery(id+"F20.wireOp",EDGE,"E112.right");Q6=makeQuery(id+"F20.imprint","IMPRINT",FACE,{"disambiguationData":[TD([[makeQuery(id+"F20.imprint","IMPRINT",EDGE,{"derivedFrom":subQ0}),1.0]])]});}
            var Q7;
            {var subQ1=sQuery(id+"F20.wireOp",EDGE,"E112.bottom");var subQ3=sQuery(id+"F20.wireOp",EDGE,"E113.bottom");var subQ4=makeQuery(id+"F20.imprint","INTERSECT",VERTEX,{"derivedFrom":[subQ1,subQ3]});Q7=makeQuery(id+"F20.imprint","IMPRINT",FACE,{"disambiguationData":[TD([[makeQuery(id+"F20.imprint","IMPRINT",EDGE,{"disambiguationData":[TD([[subQ4,-1.0]])],"derivedFrom":subQ3}),1.0]])]});}
            var Q8;
            {var subQ0=sQuery(id+"F20.wireOp",EDGE,"E113.right");Q8=makeQuery(id+"F20.imprint","IMPRINT",FACE,{"disambiguationData":[TD([[makeQuery(id+"F20.imprint","IMPRINT",EDGE,{"derivedFrom":subQ0}),1.0]])]});}
            var Q9;
            Q9=makeQuery(id+"F20.imprint","IMPRINT",FACE,{"disambiguationData":[TD([[makeQuery(id+"F20.imprint","IMPRINT",EDGE,{"derivedFrom":sQuery(id+"F20.wireOp",EDGE,"E113.right")}),-1.0]])]});
            var Q10;
            {var subQ0=sQuery(id+"F20.wireOp",EDGE,"E114.right");Q10=makeQuery(id+"F20.imprint","IMPRINT",FACE,{"disambiguationData":[TD([[makeQuery(id+"F20.imprint","IMPRINT",EDGE,{"derivedFrom":subQ0}),-1.0]])]});}
            var Q11;
            {var subQ5=sQuery(id+"F20.wireOp",EDGE,"E116.left");Q11=makeQuery(id+"F20.imprint","IMPRINT",FACE,{"disambiguationData":[TD([[makeQuery(id+"F20.imprint","IMPRINT",EDGE,{"derivedFrom":subQ5}),1.0]])]});}
            var Q12;
            Q12=makeQuery(id+"F20.imprint","IMPRINT",FACE,{"disambiguationData":[TD([[makeQuery(id+"F20.imprint","IMPRINT",EDGE,{"derivedFrom":sQuery(id+"F20.wireOp",EDGE,"E116.left")}),-1.0]])]});
            var Q13;
            {var subQ0=sQuery(id+"F20.wireOp",EDGE,"E117.left");Q13=makeQuery(id+"F20.imprint","IMPRINT",FACE,{"disambiguationData":[TD([[makeQuery(id+"F20.imprint","IMPRINT",EDGE,{"derivedFrom":subQ0}),-1.0]])]});}
            var Q14;
            {var subQ0=sQuery(id+"F20.wireOp",EDGE,"E118.0.1.0");Q14=makeQuery(id+"F20.imprint","IMPRINT",FACE,{"disambiguationData":[TD([[makeQuery(id+"F20.imprint","IMPRINT",EDGE,{"derivedFrom":subQ0}),-1.0]])]});}
            var Q15;
            {var subQ5=makeQuery(id+"F0.imprint","IMPRINT",EDGE,{"derivedFrom":sQuery(id+"F0.wireOp",EDGE,"E27")});Q15=makeQuery(id+"F20.imprint","IMPRINT",FACE,{"disambiguationData":[TD([[makeQuery(id+"F20.imprint","IMPRINT",EDGE,{"derivedFrom":subQ5}),-1.0]])]});}
            var Q16;
            {var subQ0=sQuery(id+"F20.wireOp",EDGE,"E118.0.3.2");Q16=makeQuery(id+"F20.imprint","IMPRINT",FACE,{"disambiguationData":[TD([[makeQuery(id+"F20.imprint","IMPRINT",EDGE,{"derivedFrom":subQ0}),-1.0]])]});}
            var Q17;
            {var subQ0=sQuery(id+"F20.wireOp",EDGE,"E119.6.0.4");Q17=makeQuery(id+"F20.imprint","IMPRINT",FACE,{"disambiguationData":[TD([[makeQuery(id+"F20.imprint","IMPRINT",EDGE,{"derivedFrom":subQ0}),-1.0]])]});}
            var Q18;
            {var subQ4=makeQuery(id+"F0.imprint","IMPRINT",EDGE,{"derivedFrom":sQuery(id+"F0.wireOp",EDGE,"E49")});var subQ6=makeQuery(id+"F0.imprint","IMPRINT",EDGE,{"derivedFrom":sQuery(id+"F0.wireOp",EDGE,"E50")});var subQ8=makeQuery(id+"F20.imprint","INTERSECT",VERTEX,{"derivedFrom":[subQ4,subQ6]});Q18=makeQuery(id+"F20.imprint","IMPRINT",FACE,{"disambiguationData":[TD([[makeQuery(id+"F20.imprint","IMPRINT",EDGE,{"disambiguationData":[TD([[subQ8,-1.0]])],"derivedFrom":subQ6}),-1.0]])]});}
            var Q19;
            Q19=makeQuery(id+"F20.imprint","IMPRINT",FACE,{"disambiguationData":[TD([[makeQuery(id+"F20.imprint","IMPRINT",EDGE,{"derivedFrom":sQuery(id+"F20.wireOp",EDGE,"E120.bottom")}),-1.0]])]});
            var Q20;
            Q20=makeQuery(id+"F20.imprint","IMPRINT",FACE,{"disambiguationData":[TD([[makeQuery(id+"F20.imprint","IMPRINT",EDGE,{"derivedFrom":sQuery(id+"F20.wireOp",EDGE,"E120.right")}),1.0]])]});
            var Q21;
            {var subQ2=sQuery(id+"F20.wireOp",EDGE,"E121.1.0.1");Q21=makeQuery(id+"F20.imprint","IMPRINT",FACE,{"disambiguationData":[TD([[makeQuery(id+"F20.imprint","IMPRINT",EDGE,{"derivedFrom":subQ2}),1.0]])]});}
            var Q22;
            {var subQ2=sQuery(id+"F20.wireOp",EDGE,"E121.2.0.1");Q22=makeQuery(id+"F20.imprint","IMPRINT",FACE,{"disambiguationData":[TD([[makeQuery(id+"F20.imprint","IMPRINT",EDGE,{"derivedFrom":subQ2}),1.0]])]});}
            var Q23;
            Q23=makeQuery(id+"F20.imprint","IMPRINT",FACE,{"disambiguationData":[TD([[makeQuery(id+"F20.imprint","IMPRINT",EDGE,{"derivedFrom":sQuery(id+"F20.wireOp",EDGE,"E121.3.0.1")}),1.0]])]});
            var Q24;
            Q24=makeQuery(id+"F20.imprint","IMPRINT",FACE,{"disambiguationData":[TD([[makeQuery(id+"F20.imprint","IMPRINT",EDGE,{"derivedFrom":sQuery(id+"F20.wireOp",EDGE,"E121.4.0.1")}),1.0]])]});
            var Q25;
            {var subQ0=sQuery(id+"F20.wireOp",EDGE,"E123.left");Q25=makeQuery(id+"F20.imprint","IMPRINT",FACE,{"disambiguationData":[TD([[makeQuery(id+"F20.imprint","IMPRINT",EDGE,{"derivedFrom":subQ0}),1.0]])]});}
            var Q26;
            {var subQ0=sQuery(id+"F20.wireOp",EDGE,"E116.bottom");var subQ1=sQuery(id+"F20.wireOp",EDGE,"E115.bottom");var subQ2=makeQuery(id+"F20.imprint","INTERSECT",VERTEX,{"derivedFrom":[subQ1,subQ0]});Q26=makeQuery(id+"F20.imprint","IMPRINT",FACE,{"disambiguationData":[TD([[makeQuery(id+"F20.imprint","IMPRINT",EDGE,{"disambiguationData":[TD([[subQ2,-1.0]])],"derivedFrom":subQ1}),1.0]])]});}
            var Q27;
            Q27=sQuery(id+"F20.wireOp",EDGE,"E123.top");
            var Q28;
            Q28=sQuery(id+"F20.wireOp",EDGE,"E122.top");
            var Q29;
            Q29=sQuery(id+"F20.wireOp",EDGE,"E107.bottom");
            var Q30;
            Q30=sQuery(id+"F20.wireOp",EDGE,"E108.bottom");
            var Q31;
            Q31=sQuery(id+"F20.wireOp",EDGE,"E109.bottom");
            var Q32;
            Q32=sQuery(id+"F20.wireOp",EDGE,"E110.bottom");
            var Q33;
            Q33=sQuery(id+"F20.wireOp",EDGE,"E111.bottom");
            var Q34;
            Q34=sQuery(id+"F20.wireOp",EDGE,"E112.bottom");
            var Q35;
            Q35=sQuery(id+"F20.wireOp",EDGE,"E113.bottom");
            var Q36;
            Q36=sQuery(id+"F20.wireOp",EDGE,"E114.bottom");
            var Q37;
            Q37=sQuery(id+"F20.wireOp",EDGE,"E116.bottom");
            var Q38;
            Q38=sQuery(id+"F20.wireOp",EDGE,"E115.bottom");
            var Q39;
            Q39=sQuery(id+"F20.wireOp",EDGE,"E117.bottom");
            var Q40;
            Q40=sQuery(id+"F20.wireOp",EDGE,"E118.1.1.2");
            var Q41;
            Q41=sQuery(id+"F20.wireOp",EDGE,"E118.1.2.2");
            var Q42;
            Q42=sQuery(id+"F20.wireOp",EDGE,"E118.0.3.2");
            var Q43;
            Q43=sQuery(id+"F20.wireOp",EDGE,"E119.6.2.4");
            var Q44;
            Q44=sQuery(id+"F20.wireOp",EDGE,"E119.6.1.5");
            var Q45;
            Q45=sQuery(id+"F20.wireOp",EDGE,"E121.5.0.0");
            var Q46;
            Q46=sQuery(id+"F20.wireOp",EDGE,"E121.4.0.0");
            var Q47;
            Q47=sQuery(id+"F20.wireOp",EDGE,"E121.1.0.0");
            var Q48;
            Q48=sQuery(id+"F20.wireOp",EDGE,"E121.2.0.0");
            var Q49;
            Q49=sQuery(id+"F20.wireOp",EDGE,"E120.bottom");
            var Q50;
            Q50=sQuery(id+"F20.wireOp",EDGE,"E121.3.0.0");
            extrude(context, id + "F21", {"entities" : qUnion([Q0, Q1, Q2, Q3, Q4, Q5, Q6, Q7, Q8, Q9, Q10, Q11, Q12, Q13, Q14, Q15, Q16, Q17, Q18, Q19, Q20, Q21, Q22, Q23, Q24, Q25, Q26]), "surfaceEntities" : qUnion([Q27, Q28, Q29, Q30, Q31, Q32, Q33, Q34, Q35, Q36, Q37, Q38, Q39, Q40, Q41, Q42, Q43, Q44, Q45, Q46, Q47, Q48, Q49, Q50]), "depth" : 2133.6 * mm, "offsetDistance" : 25.4 * mm});
        }
    });
